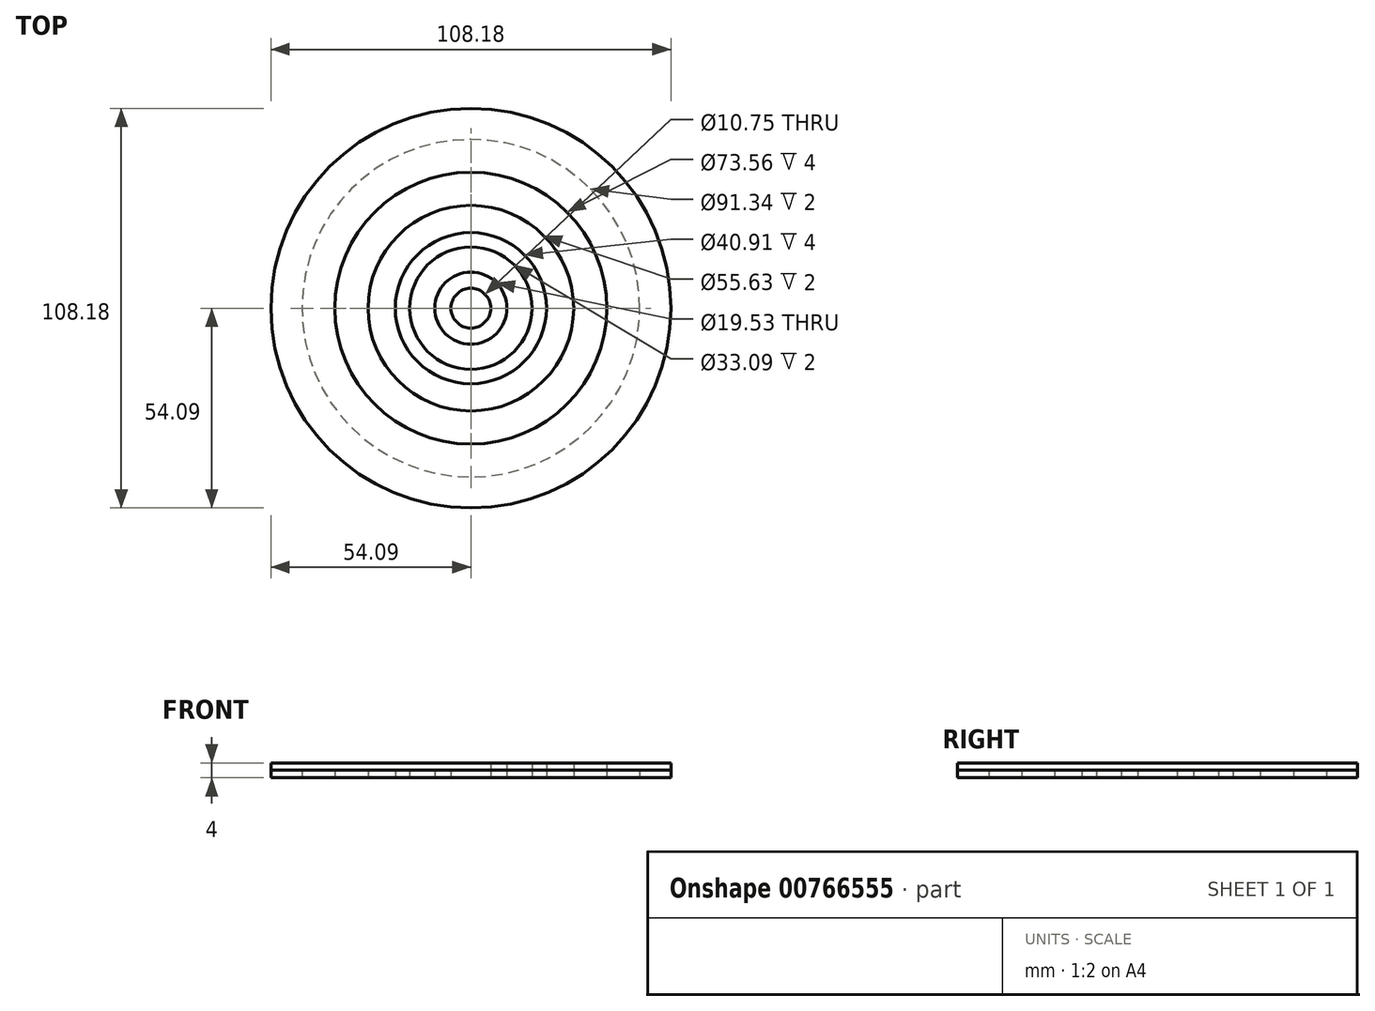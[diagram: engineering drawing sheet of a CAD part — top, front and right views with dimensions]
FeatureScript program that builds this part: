
annotation { "Feature Type Name" : "Feature", "Feature Type Description" : "" }
export const myFeature = defineFeature(function(context is Context, id is Id, definition is map)
    precondition{}
    {
        {
            var Q0;
            Q0=qCreatedBy(makeId("Top.planeOp"),FACE);
            var sketch = newSketch(context, id + "F0", { "sketchPlane" : qUnion([Q0])});
            skCircle(sketch, "E0", {"center": v(0, 0) * mm, "radius": 54.1 * mm});
            skCircle(sketch, "E1", {"center": v(0, 0) * mm, "radius": 36.78 * mm});
            skCircle(sketch, "E2", {"center": v(0, 0) * mm, "radius": 20.45 * mm});
            skCircle(sketch, "E3", {"center": v(0, 0) * mm, "radius": 9.76 * mm});
            skCircle(sketch, "E4", {"center": v(0, 0) * mm, "radius": 5.38 * mm});
            skCircle(sketch, "E5", {"center": v(0, 0) * mm, "radius": 16.55 * mm});
            skCircle(sketch, "E6", {"center": v(0, 0) * mm, "radius": 27.82 * mm});
            skCircle(sketch, "E7", {"center": v(0, 0) * mm, "radius": 45.67 * mm});
            skSolve(sketch);
        }
        {
            var Q0;
            Q0=makeQuery(id+"F0.imprint","IMPRINT",FACE,{"disambiguationData":[TD([[makeQuery(id+"F0.imprint","IMPRINT",EDGE,{"derivedFrom":sQuery(id+"F0.wireOp",EDGE,"E3")}),1.0]])]});
            var Q1;
            Q1=makeQuery(id+"F0.imprint","IMPRINT",FACE,{"disambiguationData":[TD([[makeQuery(id+"F0.imprint","IMPRINT",EDGE,{"derivedFrom":sQuery(id+"F0.wireOp",EDGE,"E1")}),1.0]])]});
            var Q2;
            Q2=makeQuery(id+"F0.imprint","IMPRINT",FACE,{"disambiguationData":[TD([[makeQuery(id+"F0.imprint","IMPRINT",EDGE,{"derivedFrom":sQuery(id+"F0.wireOp",EDGE,"E2")}),1.0]])]});
            var Q3;
            Q3=makeQuery(id+"F0.imprint","IMPRINT",FACE,{"disambiguationData":[TD([[makeQuery(id+"F0.imprint","IMPRINT",EDGE,{"derivedFrom":sQuery(id+"F0.wireOp",EDGE,"E0")}),1.0]])]});
            extrude(context, id + "F1", {"entities" : qUnion([Q0, Q1, Q2, Q3]), "depth" : 2 * mm, "offsetDistance" : 25 * mm});
        }
        {
            var Q0;
            Q0 = qSketchRegion(id + "F0", true);
            var Q1;
            Q1=makeQuery(id+"F0.imprint","IMPRINT",FACE,{"disambiguationData":[TD([[makeQuery(id+"F0.imprint","IMPRINT",EDGE,{"derivedFrom":sQuery(id+"F0.wireOp",EDGE,"E1")}),-1.0]])]});
            var Q2;
            Q2=makeQuery(id+"F0.imprint","IMPRINT",FACE,{"disambiguationData":[TD([[makeQuery(id+"F0.imprint","IMPRINT",EDGE,{"derivedFrom":sQuery(id+"F0.wireOp",EDGE,"E2")}),-1.0]])]});
            var Q3;
            Q3=makeQuery(id+"F0.imprint","IMPRINT",FACE,{"disambiguationData":[TD([[makeQuery(id+"F0.imprint","IMPRINT",EDGE,{"derivedFrom":sQuery(id+"F0.wireOp",EDGE,"E3")}),-1.0]])]});
            var Q4;
            Q4=makeQuery(id+"F0.imprint","IMPRINT",FACE,{"disambiguationData":[TD([[makeQuery(id+"F0.imprint","IMPRINT",EDGE,{"derivedFrom":sQuery(id+"F0.wireOp",EDGE,"E4")}),1.0]])]});
            extrude(context, id + "F2", {"entities" : qUnion([Q0, Q1, Q2, Q3, Q4]), "depth" : 4 * mm, "offsetDistance" : 25 * mm});
        }
    });
